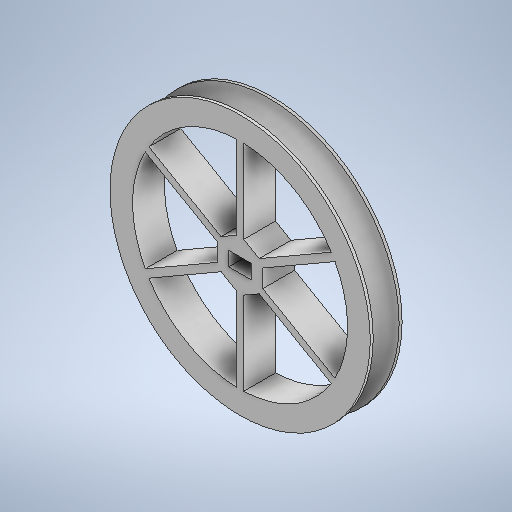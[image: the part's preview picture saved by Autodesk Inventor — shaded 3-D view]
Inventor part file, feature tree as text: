
AUTODESK INVENTOR PART (.ipt)
format: ipt  version: 2025.3 (Build 293356000, 356)  size: 326,144 bytes
history: native  units: mm
features: sketch x4, extrude x3, other x1, pattern_circular x1
ambient origin geometry x8: Origin, YZ Plane, XZ Plane, XY Plane, X Axis, Y Axis, Z Axis, Center Point
bodies: Body1 (feature_tree)
feature tree (9):
  other  "ソリッド1"
  extrude  "ハブ"  Depth=7.0mm
  extrude  "スポーク"  Depth=5.0mm
  pattern_circular  "円形状パターン1"  Angle=90.0deg  [1 undecoded]
  extrude  "軸穴"  Depth=10.0mm TaperAngle=0.0deg
  sketch  "スケッチ1"
  sketch  "スケッチ3"
  sketch  "スケッチ4"
  sketch  "スケッチ5"
note: 1 required parameter value undecoded (feature->parameter linkage not recoverable at this tier; creation-order binding heuristic only, values carry confidence <= 0.55)
